# Revit family: Shower_Arm-Rain-American_Standard-1660.103_Series
name_source: partatom
category: Plumbing Fixtures
units: mm (PartAtom-declared; Revit-internal decimal feet)

## family parameters
Always vertical = No
Cut with Voids When Loaded = No
OmniClass Number = 23.45.05.14.17
OmniClass Title = Showers
Part Type = Normal
Room Calculation Point = No
Round Connector Dimension = Use Diameter
Shared = Yes
Work Plane-Based = Yes

## types (4) — shared parameters
Assembly Code = D2010710
CW Connection = Yes
CWFU = 3
Default Elevation = 0"
Description = 3" Ceiling Mount Shower Arm
HW Connection = Yes
HWFU = 3
Height = 3"
Installation Type = Ceiling Mounted
Length = 2 1/2"
Manufacturer = American Standard
Price = Prices may vary. Please consult Manufacturer Representative for most up-to-date price list.
Product Documentation Link = https://www.americanstandard-us.com
Product Page URL = https://www.americanstandard-us.com
Revised Date = 05/11/2021
URL = https://www.americanstandard-us.com
Vent Connection = No
WFU = 4
Waste Connection = No
Water Connection Diameter = 1/2"
Water Connection Radius = 1/4"
Width = 7/8"

## per-type parameters (varying)
| type | Finish | Material |
| 1660.103.002 | Brass-American Standard-002-Polished Chrome | Brass-American Standard-002-Polished Chrome |
| 1660.103.295 | Brass-American Standard-295-Brushed Nickel | Brass-American Standard-295-Brushed Nickel |
| 1660.103.013 | Brass-American Standard-013-Polished Nickel | Brass-American Standard-013-Polished Nickel |
| 1660.103.278 | Brass-American Standard-278-Legacy Bronze | Brass-American Standard-278-Legacy Bronze |

note: column(s) folded — value = type name in every type: Model

## geometry (parser evidence)
native form markers: Sweep x3
no freeform markers — native parametric forms only
